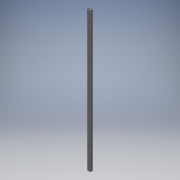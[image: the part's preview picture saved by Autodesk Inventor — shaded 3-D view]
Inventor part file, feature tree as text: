
AUTODESK INVENTOR PART (.ipt)
format: ipt  version: 2017.3 (Build 213256000, 256)  size: 169,984 bytes
history: native  units: mm
features: extrude x3, sketch x3, pattern_linear x2
ambient origin geometry x8: Origin, YZ Plane, XZ Plane, XY Plane, X Axis, Y Axis, Z Axis, Center Point
bodies: Solid1 (feature_tree)
feature tree (8):
  extrude  "Extrusion1"  Depth=6.5mm
  extrude  "Extrusion2"  Depth=1.0mm
  pattern_linear  "Rectangular Pattern1"  Spacing1=0.704mm  [1 undecoded]
  extrude  "Extrusion3"  Depth=420.0mm TaperAngle=0.0deg
  pattern_linear  "Rectangular Pattern2"  Spacing1=3.2mm  [1 undecoded]
  sketch  "Sketch1"  dims[d0=9.0mm d1=6.5mm]
  sketch  "Sketch2"  dims[d2=1.0mm d3=2.0mm d4=1.0mm]
  sketch  "Sketch3"  dims[d5=0.329mm d6=0.704mm d7=420.0mm d8=0.0mm d9=3.2mm d10=470.0mm d11=0.0mm d12=230.0mm d14=20.0mm d15=6.0mm d16=3.5mm d17=0.0mm d18=230.0mm d20=20.0mm]
note: 2 required parameter values undecoded (feature->parameter linkage not recoverable at this tier; creation-order binding heuristic only, values carry confidence <= 0.55)
